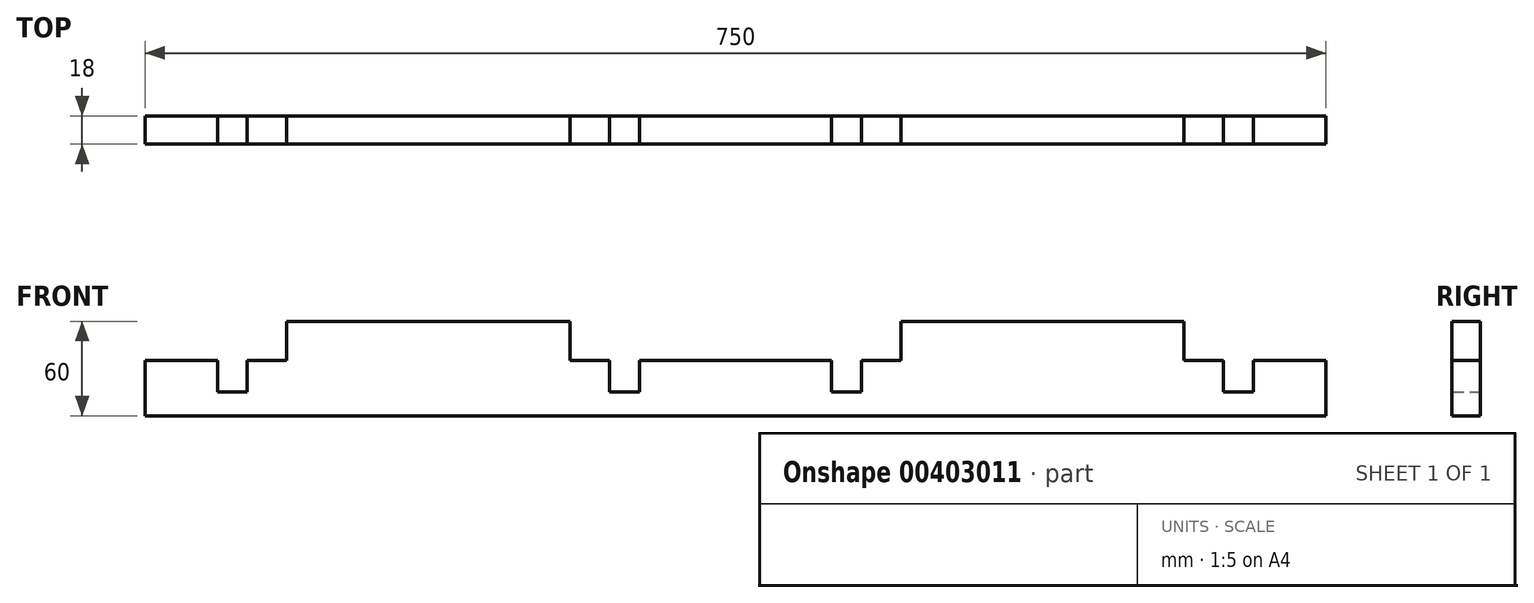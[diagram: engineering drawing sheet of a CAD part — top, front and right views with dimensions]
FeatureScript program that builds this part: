
annotation { "Feature Type Name" : "Feature", "Feature Type Description" : "" }
export const myFeature = defineFeature(function(context is Context, id is Id, definition is map)
    precondition{}
    {
        {
            var Q0;
            Q0=qCreatedBy(makeId("Front.planeOp"),FACE);
            var sketch = newSketch(context, id + "F0", { "sketchPlane" : qUnion([Q0])});
            skLineSegment(sketch, "E0.top", {"start": v(0, 35) * mm, "end": v(46, 35) * mm});
            skLineSegment(sketch, "E0.left", {"start": v(0, 0) * mm, "end": v(0, 35) * mm});
            skLineSegment(sketch, "E0.right", {"start": v(750, 0) * mm, "end": v(750, 35) * mm});
            skLineSegment(sketch, "E1.top", {"start": v(90, 60) * mm, "end": v(270, 60) * mm});
            skLineSegment(sketch, "E1.left", {"start": v(90, 35) * mm, "end": v(90, 60) * mm});
            skLineSegment(sketch, "E1.right", {"start": v(270, 35) * mm, "end": v(270, 60) * mm});
            skLineSegment(sketch, "E2.top", {"start": v(480, 60) * mm, "end": v(660, 60) * mm});
            skLineSegment(sketch, "E2.left", {"start": v(480, 35) * mm, "end": v(480, 60) * mm});
            skLineSegment(sketch, "E2.right", {"start": v(660, 35) * mm, "end": v(660, 60) * mm});
            skLineSegment(sketch, "E3.trimOffspring", {"start": v(270, 35) * mm, "end": v(295, 35) * mm});
            skLineSegment(sketch, "E4.trimOffspring", {"start": v(660, 35) * mm, "end": v(685, 35) * mm});
            skPoint(sketch, "E5.firstSnap0", {"position": v(46, 35) * mm});
            skLineSegment(sketch, "E5.top", {"start": v(46, 15) * mm, "end": v(65, 15) * mm});
            skLineSegment(sketch, "E5.left", {"start": v(46, 35) * mm, "end": v(46, 15) * mm});
            skLineSegment(sketch, "E5.right", {"start": v(65, 35) * mm, "end": v(65, 15) * mm});
            skLineSegment(sketch, "E6.top", {"start": v(685, 15) * mm, "end": v(704, 15) * mm});
            skLineSegment(sketch, "E6.left", {"start": v(685, 35) * mm, "end": v(685, 15) * mm});
            skLineSegment(sketch, "E6.right", {"start": v(704, 35) * mm, "end": v(704, 15) * mm});
            skLineSegment(sketch, "E7.trimOffspring", {"start": v(65, 35) * mm, "end": v(90, 35) * mm});
            skLineSegment(sketch, "E8.trimOffspring", {"start": v(704, 35) * mm, "end": v(750, 35) * mm});
            skLineSegment(sketch, "E9", {"start": v(0, 0) * mm, "end": v(750, 0) * mm});
            skLineSegment(sketch, "E10.left", {"start": v(295, 35) * mm, "end": v(295, 15) * mm});
            skLineSegment(sketch, "E10.right", {"start": v(455, 35) * mm, "end": v(455, 15) * mm});
            skLineSegment(sketch, "E11.trimOffspring", {"start": v(455, 35) * mm, "end": v(480, 35) * mm});
            skLineSegment(sketch, "E12.bottom", {"start": v(314, 35) * mm, "end": v(436, 35) * mm});
            skLineSegment(sketch, "E12.left", {"start": v(314, 35) * mm, "end": v(314, 15) * mm});
            skLineSegment(sketch, "E12.right", {"start": v(436, 35) * mm, "end": v(436, 15) * mm});
            skLineSegment(sketch, "E13", {"start": v(295, 15) * mm, "end": v(314, 15) * mm});
            skLineSegment(sketch, "E14.trimOffspring", {"start": v(436, 15) * mm, "end": v(455, 15) * mm});
            skSolve(sketch);
        }
        {
            var Q0;
            Q0=makeQuery(id+"F0.imprint","IMPRINT",FACE,{"disambiguationData":[TD([[makeQuery(id+"F0.imprint","IMPRINT",EDGE,{"derivedFrom":sQuery(id+"F0.wireOp",EDGE,"E0.top")}),-1.0]])]});
            extrude(context, id + "F1", {"entities" : qUnion([Q0]), "depth" : 18 * mm});
        }
    });
